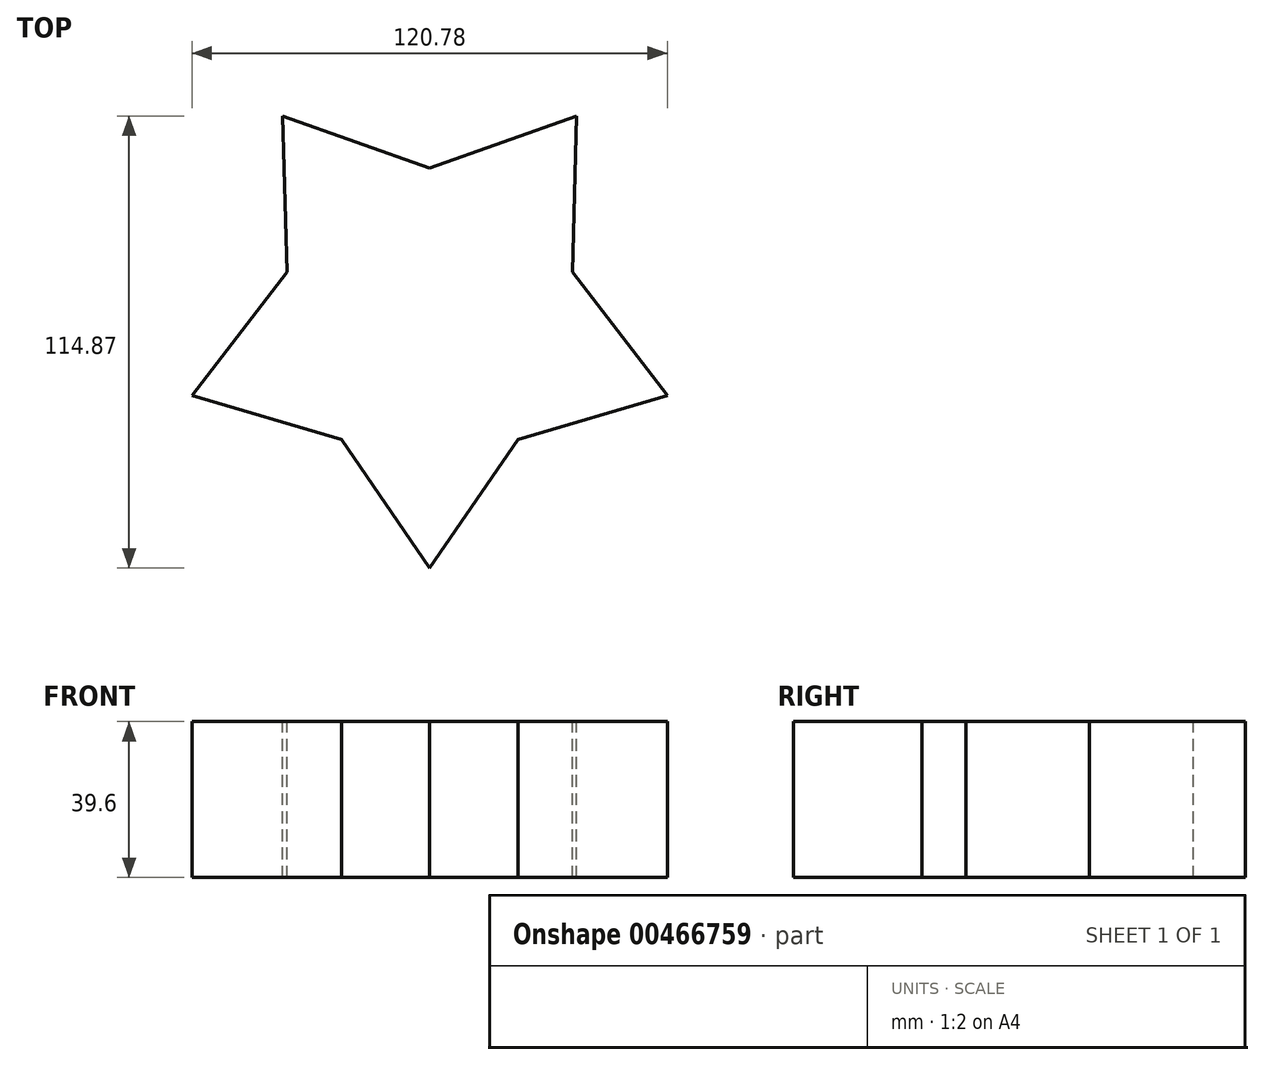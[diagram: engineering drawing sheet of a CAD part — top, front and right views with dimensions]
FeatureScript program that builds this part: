
annotation { "Feature Type Name" : "Feature", "Feature Type Description" : "" }
export const myFeature = defineFeature(function(context is Context, id is Id, definition is map)
    precondition{}
    {
        {
            var Q0;
            Q0=qCreatedBy(makeId("Top.planeOp"),FACE);
            var sketch = newSketch(context, id + "F0", { "sketchPlane" : qUnion([Q0])});
            skCircle(sketch, "E0", {"center": v(0, 0) * mm, "radius": 63.5 * mm});
            skCircle(sketch, "E1.cCircle", {"center": v(0, 0) * mm, "radius": 63.5 * mm, "construction": true});
            skLineSegment(sketch, "E1.0", {"start": v(-37.32, 51.37) * mm, "end": v(37.32, 51.37) * mm});
            skLineSegment(sketch, "E1.1", {"start": v(37.32, 51.37) * mm, "end": v(60.4, -19.62) * mm});
            skLineSegment(sketch, "E1.2", {"start": v(60.4, -19.62) * mm, "end": v(0, -63.5) * mm});
            skLineSegment(sketch, "E1.3", {"start": v(0, -63.5) * mm, "end": v(-60.4, -19.62) * mm});
            skLineSegment(sketch, "E1.4", {"start": v(-60.4, -19.62) * mm, "end": v(-37.32, 51.37) * mm});
            skLineSegment(sketch, "E2", {"start": v(30.2, -41.56) * mm, "end": v(0, 0) * mm});
            skPoint(sketch, "E3", {"position": v(-60.4, 19.62) * mm});
            skLineSegment(sketch, "E4", {"start": v(-60.4, 19.62) * mm, "end": v(-37.32, 51.37) * mm});
            skLineSegment(sketch, "E5", {"start": v(-60.4, -19.62) * mm, "end": v(-60.4, 19.62) * mm});
            skLineSegment(sketch, "E6", {"start": v(-60.4, 19.62) * mm, "end": v(0, 0) * mm});
            skPoint(sketch, "E7", {"position": v(-36.24, 11.77) * mm});
            skLineSegment(sketch, "E8", {"start": v(-37.32, 51.37) * mm, "end": v(-36.24, 11.77) * mm});
            skLineSegment(sketch, "E9", {"start": v(-60.4, -19.62) * mm, "end": v(-36.24, 11.77) * mm});
            skLineSegment(sketch, "E10.1.0", {"start": v(-60.4, -19.62) * mm, "end": v(-22.4, -30.82) * mm});
            skLineSegment(sketch, "E10.1.1", {"start": v(0, -63.5) * mm, "end": v(-22.4, -30.82) * mm});
            skLineSegment(sketch, "E10.2.0", {"start": v(0, -63.5) * mm, "end": v(22.4, -30.82) * mm});
            skLineSegment(sketch, "E10.2.1", {"start": v(60.4, -19.62) * mm, "end": v(22.4, -30.82) * mm});
            skLineSegment(sketch, "E10.3.0", {"start": v(60.4, -19.62) * mm, "end": v(36.24, 11.77) * mm});
            skLineSegment(sketch, "E10.3.1", {"start": v(37.32, 51.37) * mm, "end": v(36.24, 11.77) * mm});
            skLineSegment(sketch, "E10.4.0", {"start": v(37.32, 51.37) * mm, "end": v(0, 38.1) * mm});
            skLineSegment(sketch, "E10.4.1", {"start": v(-37.32, 51.37) * mm, "end": v(0, 38.1) * mm});
            skSolve(sketch);
        }
        {
            var Q0;
            {var subQ4=sQuery(id+"F0.wireOp",EDGE,"E8");Q0=makeQuery(id+"F0.imprint","IMPRINT",FACE,{"disambiguationData":[TD([[makeQuery(id+"F0.imprint","IMPRINT",EDGE,{"derivedFrom":subQ4}),1.0]])]});}
            var Q1;
            {var subQ0=sQuery(id+"F0.wireOp",EDGE,"E9");Q1=makeQuery(id+"F0.imprint","IMPRINT",FACE,{"disambiguationData":[TD([[makeQuery(id+"F0.imprint","IMPRINT",EDGE,{"derivedFrom":subQ0}),-1.0]])]});}
            extrude(context, id + "F1", {"entities" : qUnion([Q0, Q1]), "oppositeDirection" : true, "depth" : 39.6 * mm});
        }
    });
